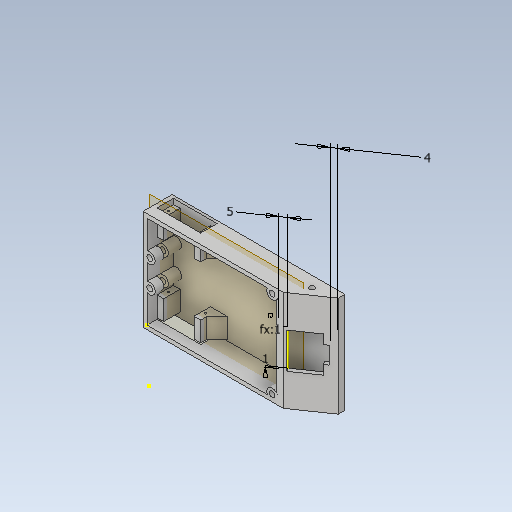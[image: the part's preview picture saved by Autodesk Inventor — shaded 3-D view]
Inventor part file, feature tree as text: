
AUTODESK INVENTOR PART (.ipt)
format: ipt  version: 2020 (Build 240168000, 168)  size: 332,288 bytes
history: native  units: mm
features: extrude x16, sketch x14, reference x11, other x8, projected_geometry x6, plane x2, hole x1, chamfer x1
ambient origin geometry x8: Origin, YZ Plane, XZ Plane, XY Plane, X Axis, Y Axis, Z Axis, Center Point
bodies: Solid1 (feature_tree)
feature tree (59):
  sketch  "Sketch1"  dims[d0=100.0mm d1=70.0mm]
  extrude  "Extrusion1"  Depth=70.0mm
  extrude  "Extrusion2"  Depth=2.0mm TaperAngle=0.0deg
  extrude  "Extrusion3"  Depth=33.0mm
  sketch  "Sketch3"  dims[d5=20.0mm d6=0.0mm d7=33.0mm]
  plane  "Work Plane1"
  extrude  "Extrusion4"  Depth=12.4mm TaperAngle=0.0deg
  hole  "Hole1"  [1 undecoded]
  sketch  "Sketch5"  dims[d11=15.0mm d12=15.0mm]
  extrude  "Extrusion5"  Depth=15.0mm
  extrude  "Extrusion6"  Depth=8.0mm
  extrude  "Extrusion7"  Depth=5.0mm TaperAngle=0.0deg
  extrude  "Extrusion8"  Depth=76.0mm TaperAngle=0.0deg
  extrude  "Extrusion9"  Depth=3.0mm TaperAngle=0.0deg
  extrude  "Extrusion10"  Depth=27.0mm
  sketch  "Sketch9"  dims[d33=5.0mm d40=41.25mm d41=0.0mm]
  sketch  "Sketch10"  dims[d42=3.0mm d43=76.0mm d44=0.0mm]
  extrude  "Extrusion12"  Depth=3.0mm
  sketch  "Sketch13"  dims[d49=21.75mm d50=0.0mm d52=27.0mm]
  extrude  "Extrusion13"  Depth=3.0mm TaperAngle=0.0deg
  extrude  "Extrusion14"  Depth=2.0mm
  sketch  "Sketch14"  dims[d53=20.0mm d54=3.0mm]
  extrude  "Extrusion15"  Depth=5.0mm
  extrude  "Extrusion16"  Depth=4.0mm
  plane  "Work Plane2"
  extrude  "Extrusion17"  Depth=1.0mm
  chamfer  "Chamfer1"  Distance=1.0mm
  sketch  "Sketch2"  dims[d2=3.0mm d3=2.0mm d4=0.0mm]
  reference  "Reference1"
  reference  "Reference2"
  reference  "Reference3"
  reference  "Reference4"
  reference  "Reference5"
  reference  "Reference6"
  reference  "Reference7"
  reference  "Reference8"
  sketch  "Sketch4"  dims[d8=12.4mm d9=30.0mm d10=0.0mm]
  reference  "Reference9"
  reference  "Reference10"
  sketch  "Sketch6"  dims[d13=15.0mm d14=15.0mm]
  sketch  "Sketch7"  dims[d15=30.0mm d16=0.0mm]
  projected_geometry  "Projected Loop1"
  sketch  "Sketch8"  dims[d17=1.5mm d18=6.0mm d19=4.0mm d20=2.0mm d21=90.0deg d22=8.0mm d23=0.0mm d32=30.0mm]
  projected_geometry  "Projected Loop2"
  sketch  "Sketch12"  dims[d45=3.0mm d46=0.0mm d47=3.0mm d48=0.0mm]
  reference  "Reference11"
  sketch  "Sketch15"  dims[d55=13.0mm d56=3.0mm d57=0.0mm d58=2.0mm d59=5.0mm d60=4.0mm d61=1.0mm d62=1.0mm d67=100.0mm d68=4.0mm d69=10.0mm d70=0.0mm d71=25.0mm d72=25.0mm d73=2.0mm d74=4.25mm d75=4.25mm d76=2.0mm d77=2.0mm d78=2.0mm d79=10.0mm d80=0.0mm d81=10.0mm d82=0.0mm d83=4.25mm d84=4.25mm d85=2.0mm d86=2.0mm d87=2.0mm d88=2.0mm d89=3.0mm d90=3.0mm d91=10.0mm d92=0.0mm d93=10.0mm d94=0.0mm d95=-10.0mm d96=3.5mm d97=0.0mm d98=8.0mm d99=2.0mm d100=45.0deg]
  projected_geometry  "Projected Loop4"
  projected_geometry  "Projected Loop5"
  projected_geometry  "Projected Loop6"
  projected_geometry  "Projected Loop7"
  other  "Assembly1"
  other  "Tower Pro MG90S Micro servo:2"
  other  "Крышка корпуса:1"
  other  "<userpath>\Desktop\3d\scanning-robot\Assembly1.iam"
  other  "Assembly1.iam"
  other  "Tower Pro MG90S Micro servo:1"
  other  "Цилиндрическое зубчатое зацепление:5"
  other  "Цилиндрическое зубчатое зацепление2:1"
note: 1 required parameter value undecoded (feature->parameter linkage not recoverable at this tier; creation-order binding heuristic only, values carry confidence <= 0.55)
